# Revit family: ROBUST_xxx-DB
name_source: partatom
category: Leuchten
units: mm (PartAtom-declared; Revit-internal decimal feet)

## family parameters
Basisbauteil = Fläche
Beim Laden mit Abzugskörper schneiden = Nein
Bemaßung runder Anschluss = Durchmesser verwenden
Gemeinsam genutzt = Nein
Lichtquelle = Ja
OmniClass-Nummer = 23.80.70.11
OmniClass-Titel = Luminaries for Internal Lighting
Raumberechnungspunkt = Nein
Teiletyp = Normal

## types (2) — shared parameters
Baugruppenkennzeichen = D5020200
Beschreibung = Anbauindustrieleuchte Schutzart IP66 für Decken-, Pendel- oder Tragschienenmontage.
Stabiles Leuchtengehäuse aus Aluminiumdruckguss, weiß, pulverbeschichtet, Farbe ähnlich
RAL9016. RIDI-LED-Module als Linearplatine ausgebildet, bestückt mit LEDs mit erhöhter
Schadgasfestigkeit. Scheibe aus Einscheibensicherheitsglas (ESG), strukturiert, über
Edelstahl-Verschlüsse am Gehäuse befestigt und mit Schrauben gesichert.
Schlagfestigkeit IK09.
Farbwiedergabeindex Ra >= 80, Farbtemperatur 4000 Kelvin (840)
Elektrische Ausführungen:
Elektronischer Konverter für LED, 230-240 Volt, 0/50/60 Hz und innen
liegender Anschlussklemme 5x2,5mm². Netzanschlussleitung ÖLFLEX 3x1,0mm²
schwarz mit offenem Ende, Länge 2m. Offene Enden mit Leuchtenklemme geschützt.
Leuchte mit integriertem 10kV-Transientenfilter entsprechend der DB-Anforderungen.
Betriebsgerät: schaltbar
Certification = CE
Emissionsform beim Rendern sichtbar = Nein
Farbfilter = 16777215
Farbtemperaturverschiebung bei Dämpfen der Lampe = <Keine Auswahl>
Height = 130 mm  [stored 0.426509 ft]
Hersteller = RIDI Leuchten GmbH
IP Rating = IP66
Lampe = LED
Length = 415 mm  [stored 1.36155 ft]
Neigungswinkel = -90,00°
URL = www.ridi.de
Von Breite des Rechtecks ausssenden = 292 mm  [stored 0.958005 ft]
Von Länge des Rechtecks aussenden = 386 mm  [stored 1.2664 ft]
Width = 415 mm  [stored 1.36155 ft]
impact protection rating (IK) = IK 09
nominal frequency = 50-60 Hz
nominal voltage = 230 V
voltage type (AC-DC-UC) = AC
weight = 7.4 kg
zero-valued in all types: Vorgabe-Ansicht

## per-type parameters (varying)
| type | Datei für fotometrisches Netz | Modell | Scheinlast | rated input power |
| ROBUST NDWS840B1500-DB | ROBUST NDWS840B1500-DB.IES | 6068020 | 118 VA | 118 |
| ROBUST NDWS840B2000-DB | ROBUST NDWS840B2000-DB.IES | 6068007 | 158 VA | 158 |

note: column(s) folded — value = type name in every type: product name

note: [stored X ft] marks values corroborated as IEEE doubles in the binary element streams (Revit-internal decimal feet)
